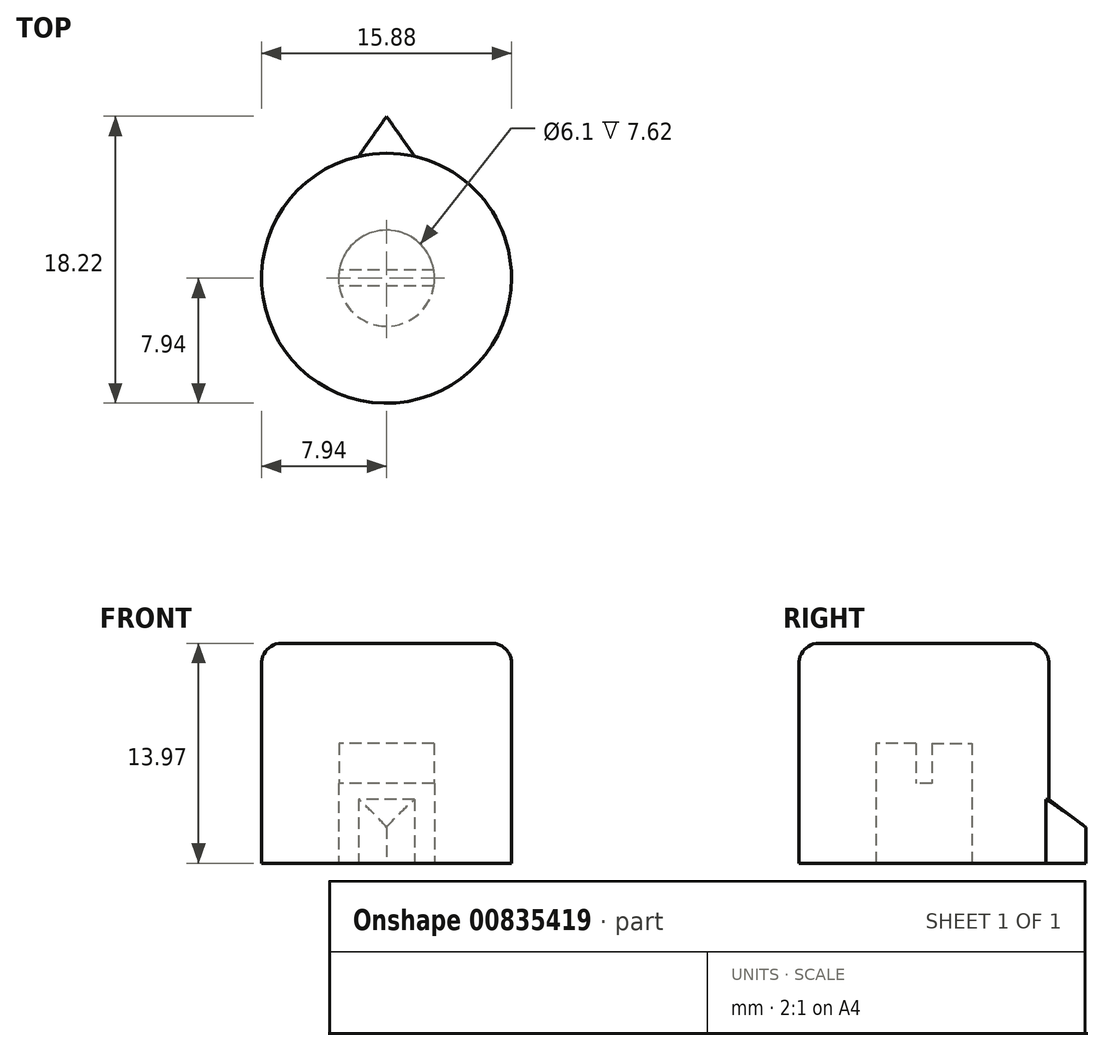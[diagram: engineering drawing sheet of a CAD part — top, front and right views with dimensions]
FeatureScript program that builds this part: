
annotation { "Feature Type Name" : "Feature", "Feature Type Description" : "" }
export const myFeature = defineFeature(function(context is Context, id is Id, definition is map)
    precondition{}
    {
        {
            var Q0;
            Q0=qCreatedBy(makeId("Top.planeOp"),FACE);
            var sketch = newSketch(context, id + "F0", { "sketchPlane" : qUnion([Q0])});
            skCircle(sketch, "E0", {"center": v(0, 0) * mm, "radius": 3.05 * mm});
            skArc(sketch, "E1", {"start": v(-1.78, 7.74) * mm, "mid": v(0, -7.94) * mm, "end": v(1.78, 7.74) * mm});
            skLineSegment(sketch, "E2", {"start": v(-1.78, 7.74) * mm, "end": v(0, 10.28) * mm});
            skLineSegment(sketch, "E3.MirrorCS", {"start": v(1.78, 7.74) * mm, "end": v(0, 10.28) * mm});
            skSolve(sketch);
        }
        {
            var Q0;
            Q0 = qSketchRegion(id + "F0", true);
            extrude(context, id + "F1", {"entities" : qUnion([Q0]), "depth" : 7.62 * mm, "offsetDistance" : 25.4 * mm});
        }
        {
            var Q0;
            Q0=makeQuery(id+"F1.opExtrude","CAP_FACE",FACE,{"disambiguationData":[OSD([sQuery(id+"F0.wireOp",EDGE,"E0"),sQuery(id+"F0.wireOp",EDGE,"E1"),sQuery(id+"F0.wireOp",EDGE,"E2"),sQuery(id+"F0.wireOp",EDGE,"E3.MirrorCS")])],"isStart":false});
            var sketch = newSketch(context, id + "F2", { "sketchPlane" : qUnion([Q0])});
            skLineSegment(sketch, "E4.bottom", {"start": v(3.3, -0.5) * mm, "end": v(-3.3, -0.5) * mm});
            skLineSegment(sketch, "E4.top", {"start": v(3.3, 0.5) * mm, "end": v(-3.3, 0.5) * mm});
            skLineSegment(sketch, "E4.left", {"start": v(3.3, -0.5) * mm, "end": v(3.3, 0.5) * mm});
            skLineSegment(sketch, "E4.right", {"start": v(-3.3, -0.5) * mm, "end": v(-3.3, 0.5) * mm});
            skPoint(sketch, "E4.middle", {"position": v(0, 0) * mm});
            skSolve(sketch);
        }
        {
            var Q0;
            Q0 = qSketchRegion(id + "F2", true);
            extrude(context, id + "F3", {"entities" : qUnion([Q0]), "operationType" : NewBodyOperationType.ADD, "oppositeDirection" : true, "depth" : 2.54 * mm, "offsetDistance" : 25.4 * mm});
        }
        {
            var Q0;
            Q0=makeQuery(id+"F3.boolean.opBoolean","MERGE",FACE,{"derivedFrom":[makeQuery(id+"F1.opExtrude","CAP_FACE",FACE,{"disambiguationData":[OSD([sQuery(id+"F0.wireOp",EDGE,"E0"),sQuery(id+"F0.wireOp",EDGE,"E1"),sQuery(id+"F0.wireOp",EDGE,"E2"),sQuery(id+"F0.wireOp",EDGE,"E3.MirrorCS")])],"isStart":false}),makeQuery(id+"F3.opExtrude","CAP_FACE",FACE,{"disambiguationData":[OSD([sQuery(id+"F2.wireOp",EDGE,"E4.bottom"),sQuery(id+"F2.wireOp",EDGE,"E4.top"),sQuery(id+"F2.wireOp",EDGE,"E4.left"),sQuery(id+"F2.wireOp",EDGE,"E4.right")])],"isStart":true})]});
            var sketch = newSketch(context, id + "F4", { "sketchPlane" : qUnion([Q0])});
            skCircle(sketch, "E5", {"center": v(0, 0) * mm, "radius": 7.94 * mm});
            skSolve(sketch);
        }
        {
            var Q0;
            Q0 = qSketchRegion(id + "F4", true);
            extrude(context, id + "F5", {"entities" : qUnion([Q0]), "operationType" : NewBodyOperationType.ADD, "depth" : 6.35 * mm, "offsetDistance" : 25.4 * mm});
        }
        {
            var Q0;
            Q0=qCreatedBy(makeId("Right.planeOp"),FACE);
            var sketch = newSketch(context, id + "F6", { "sketchPlane" : qUnion([Q0])});
            skLineSegment(sketch, "E6", {"start": v(7.94, 8.17) * mm, "end": v(7.94, 4.06) * mm});
            skLineSegment(sketch, "E7", {"start": v(10.28, 8.17) * mm, "end": v(7.94, 8.17) * mm});
            skLineSegment(sketch, "E8", {"start": v(0, 0) * mm, "end": v(0, 17.07) * mm, "construction": true});
            skLineSegment(sketch, "E9", {"start": v(10.28, 8.17) * mm, "end": v(10.28, 2.29) * mm});
            skLineSegment(sketch, "E10", {"start": v(10.28, 2.29) * mm, "end": v(7.94, 4.06) * mm});
            skSolve(sketch);
        }
        {
            var Q0;
            Q0=makeQuery(id+"F6.imprint","IMPRINT",FACE,{"disambiguationData":[TD([[makeQuery(id+"F6.imprint","IMPRINT",EDGE,{"derivedFrom":sQuery(id+"F6.wireOp",EDGE,"E6")}),1.0]])]});
            var Q1;
            Q1=sQuery(id+"F6.wireOp",EDGE,"E8");
            revolve(context, id + "F7", {"operationType" : NewBodyOperationType.REMOVE, "surfaceOperationType" : NewSurfaceOperationType.NEW, "entities" : qUnion([Q0]), "axis" : qUnion([Q1]), "revolveType" : RevolveType.FULL, "oppositeDirection" : true});
        }
        {
            var Q0;
            Q0=makeQuery(id+"F5.opExtrude","CAP_EDGE",EDGE,{"disambiguationData":[OSD([sQuery(id+"F4.wireOp",EDGE,"E5")])],"isStart":false});
            fillet(context, id + "F8", {"entities" : qUnion([Q0]), "radius" : 1.27 * mm, "tangentPropagation" : true, "allowEdgeOverflow" : false});
        }
    });
